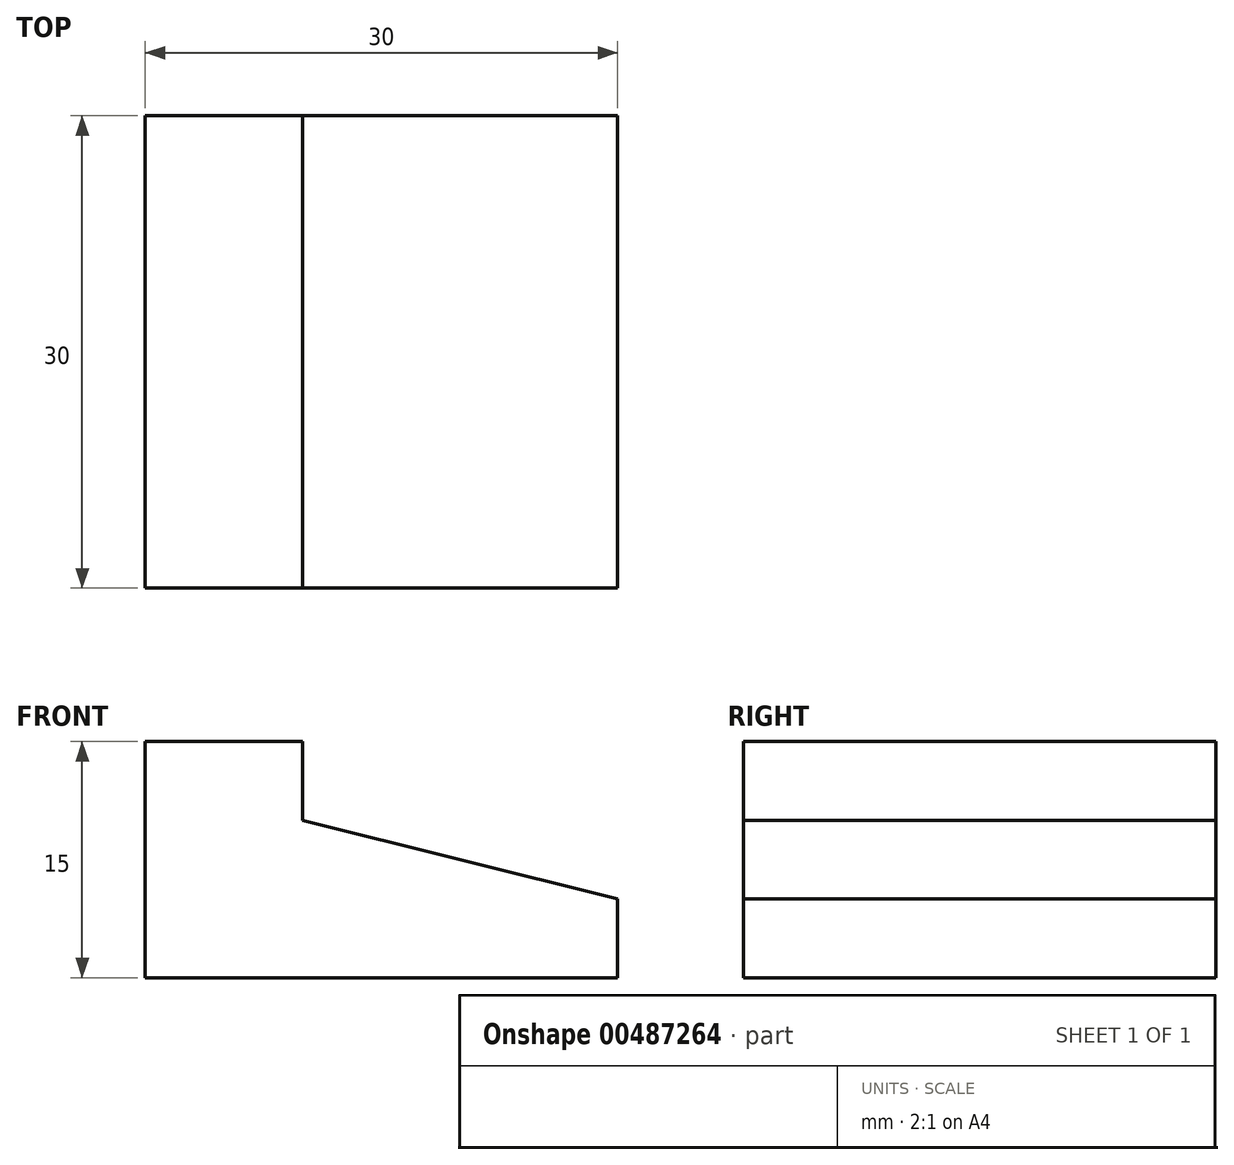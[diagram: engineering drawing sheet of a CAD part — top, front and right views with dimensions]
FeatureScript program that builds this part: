
annotation { "Feature Type Name" : "Feature", "Feature Type Description" : "" }
export const myFeature = defineFeature(function(context is Context, id is Id, definition is map)
    precondition{}
    {
        {
            var Q0;
            Q0=qCreatedBy(makeId("Top.planeOp"),FACE);
            var sketch = newSketch(context, id + "F0", { "sketchPlane" : qUnion([Q0])});
            skLineSegment(sketch, "E0.bottom", {"start": v(-18.75, 28.18) * mm, "end": v(11.25, 28.18) * mm});
            skLineSegment(sketch, "E0.top", {"start": v(-18.75, -1.82) * mm, "end": v(11.25, -1.82) * mm});
            skLineSegment(sketch, "E0.left", {"start": v(-18.75, 28.18) * mm, "end": v(-18.75, -1.82) * mm});
            skLineSegment(sketch, "E0.right", {"start": v(11.25, 28.18) * mm, "end": v(11.25, -1.82) * mm});
            skSolve(sketch);
        }
        {
            var Q0;
            Q0=makeQuery(id+"F0.imprint","IMPRINT",FACE,{"disambiguationData":[TD([[makeQuery(id+"F0.imprint","IMPRINT",EDGE,{"derivedFrom":sQuery(id+"F0.wireOp",EDGE,"E0.bottom")}),-1.0]])]});
            extrude(context, id + "F1", {"entities" : qUnion([Q0]), "depth" : 15 * mm});
        }
        {
            var Q0;
            Q0=makeQuery(id+"F1.opExtrude","SWEPT_FACE",FACE,{"disambiguationData":[OSD([sQuery(id+"F0.wireOp",EDGE,"E0.top")])]});
            var sketch = newSketch(context, id + "F2", { "sketchPlane" : qUnion([Q0])});
            skLineSegment(sketch, "E1", {"start": v(11.25, 0) * mm, "end": v(11.25, 5) * mm});
            skLineSegment(sketch, "E2", {"start": v(11.25, 5) * mm, "end": v(-8.75, 10) * mm});
            skLineSegment(sketch, "E3", {"start": v(-8.75, 10) * mm, "end": v(-8.75, 15) * mm});
            skLineSegment(sketch, "E4", {"start": v(-8.75, 15) * mm, "end": v(-18.75, 15) * mm});
            skSolve(sketch);
        }
        {
            var Q0;
            Q0 = qSketchRegion(id + "F2", true);
            var Q1;
            {var subQ0=sQuery(id+"F2.wireOp",EDGE,"E2");Q1=makeQuery(id+"F2.imprint","IMPRINT",FACE,{"disambiguationData":[TD([[makeQuery(id+"F2.imprint","IMPRINT",EDGE,{"derivedFrom":subQ0}),-1.0]])]});}
            extrude(context, id + "F3", {"entities" : qUnion([Q0, Q1]), "operationType" : NewBodyOperationType.REMOVE, "endBound" : BoundingType.THROUGH_ALL, "oppositeDirection" : true, "depth" : 25 * mm});
        }
    });
